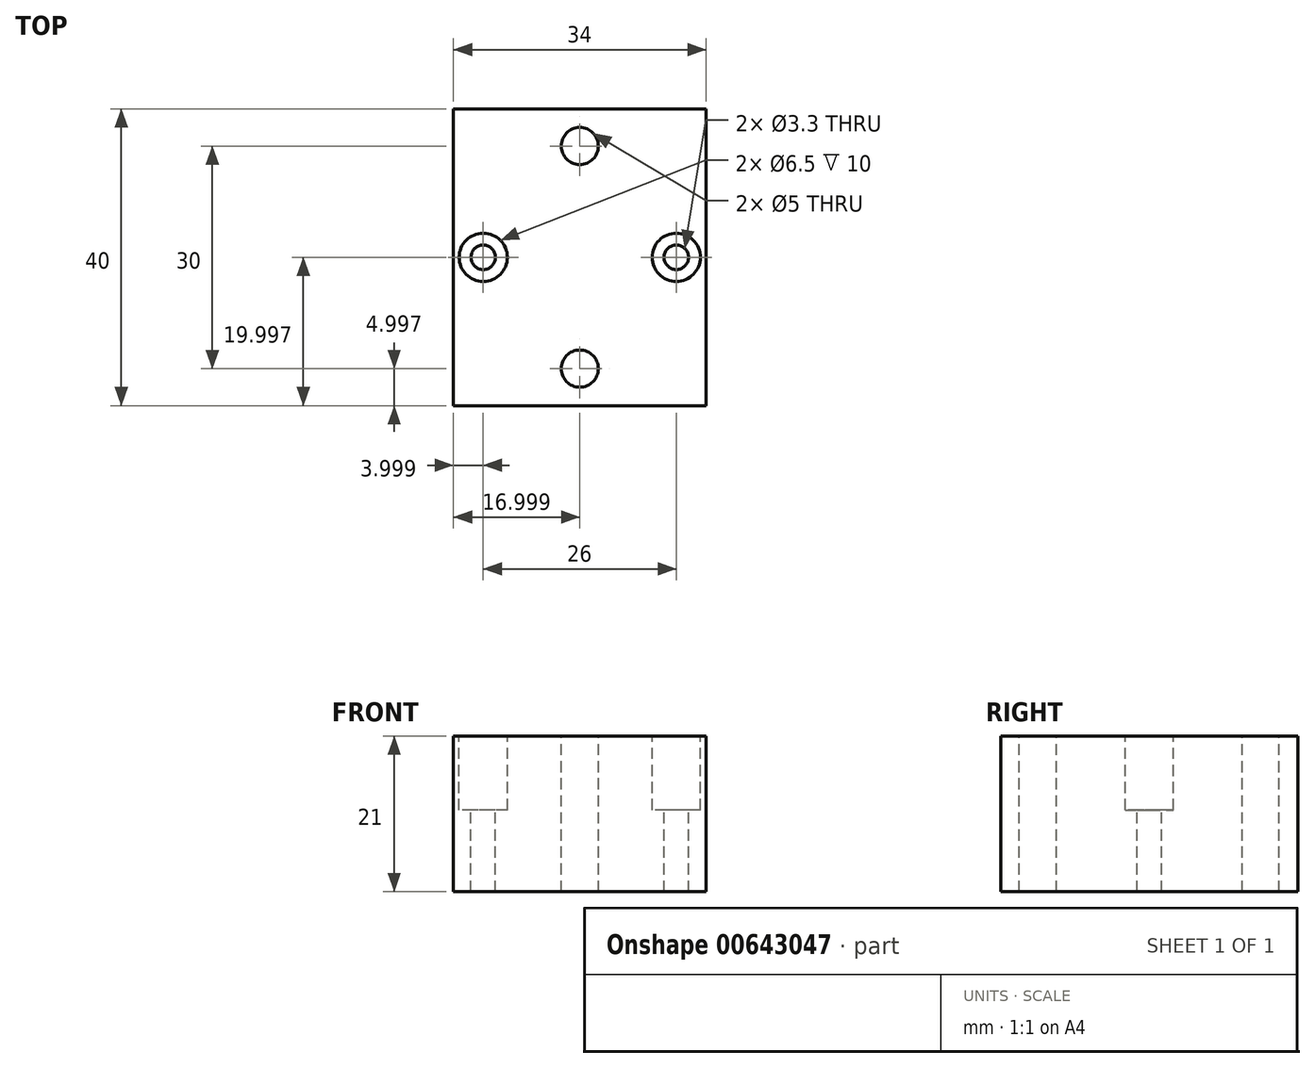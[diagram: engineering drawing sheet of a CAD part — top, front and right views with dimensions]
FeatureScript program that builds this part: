
annotation { "Feature Type Name" : "Feature", "Feature Type Description" : "" }
export const myFeature = defineFeature(function(context is Context, id is Id, definition is map)
    precondition{}
    {
        {
            var Q0;
            Q0=qCreatedBy(makeId("Top.planeOp"),FACE);
            var sketch = newSketch(context, id + "F0", { "sketchPlane" : qUnion([Q0])});
            skLineSegment(sketch, "E0.bottom", {"start": v(-36.8, -23.83) * mm, "end": v(-2.8, -23.83) * mm});
            skLineSegment(sketch, "E0.top", {"start": v(-36.8, -63.83) * mm, "end": v(-2.8, -63.83) * mm});
            skLineSegment(sketch, "E0.left", {"start": v(-36.8, -23.83) * mm, "end": v(-36.8, -63.83) * mm});
            skLineSegment(sketch, "E0.right", {"start": v(-2.8, -23.83) * mm, "end": v(-2.8, -63.83) * mm});
            skSolve(sketch);
        }
        {
            var Q0;
            Q0=makeQuery(id+"F0.imprint","IMPRINT",FACE,{"disambiguationData":[TD([[makeQuery(id+"F0.imprint","IMPRINT",EDGE,{"derivedFrom":sQuery(id+"F0.wireOp",EDGE,"E0.bottom")}),-1.0]])]});
            extrude(context, id + "F1", {"entities" : qUnion([Q0]), "depth" : 21 * mm});
        }
        {
            var Q0;
            Q0=makeQuery(id+"F1.opExtrude","CAP_FACE",FACE,{"disambiguationData":[OSD([sQuery(id+"F0.wireOp",EDGE,"E0.bottom"),sQuery(id+"F0.wireOp",EDGE,"E0.top"),sQuery(id+"F0.wireOp",EDGE,"E0.left"),sQuery(id+"F0.wireOp",EDGE,"E0.right")])],"isStart":false});
            var sketch = newSketch(context, id + "F2", { "sketchPlane" : qUnion([Q0])});
            skLineSegment(sketch, "E1", {"start": v(-19.8, -23.83) * mm, "end": v(-19.8, -63.83) * mm, "construction": true});
            skLineSegment(sketch, "E2", {"start": v(-36.8, -43.83) * mm, "end": v(-2.8, -43.83) * mm, "construction": true});
            skPoint(sketch, "E3", {"position": v(-19.8, -28.83) * mm});
            skPoint(sketch, "E4.MirrorP", {"position": v(-19.8, -58.83) * mm});
            skPoint(sketch, "E5", {"position": v(-32.8, -43.83) * mm});
            skPoint(sketch, "E6.MirrorP", {"position": v(-6.8, -43.83) * mm});
            skSolve(sketch);
        }
        {
            var Q0;
            Q0=sQuery(id+"F2.wireOp",VERTEX,"E5");
            var Q1;
            Q1=sQuery(id+"F2.wireOp",VERTEX,"E6.MirrorP");
            var Q2;
            Q2=makeQuery(id+"F1.opExtrude","SWEPT_BODY",BODY,{"disambiguationData":[OSD([sQuery(id+"F0.wireOp",EDGE,"E0.bottom"),sQuery(id+"F0.wireOp",EDGE,"E0.top"),sQuery(id+"F0.wireOp",EDGE,"E0.left"),sQuery(id+"F0.wireOp",EDGE,"E0.right")])]});
            hole(context, id + "F3", {"style" : HoleStyle.C_BORE, "endStyle" : HoleEndStyle.THROUGH, "holeDiameter" : 3.3 * mm, "cBoreDiameter" : 6.5 * mm, "cBoreDepth" : 10 * mm, "locations" : qUnion([Q0, Q1]), "scope" : qUnion([Q2]), "tappedDepth" : 12 * mm, "tapClearance" : 3});
        }
        {
            var Q0;
            Q0=sQuery(id+"F2.wireOp",VERTEX,"E3");
            var Q1;
            Q1=sQuery(id+"F2.wireOp",VERTEX,"E4.MirrorP");
            var Q2;
            Q2=makeQuery(id+"F1.opExtrude","SWEPT_BODY",BODY,{"disambiguationData":[OSD([sQuery(id+"F0.wireOp",EDGE,"E0.bottom"),sQuery(id+"F0.wireOp",EDGE,"E0.top"),sQuery(id+"F0.wireOp",EDGE,"E0.left"),sQuery(id+"F0.wireOp",EDGE,"E0.right")])]});
            hole(context, id + "F4", {"style" : HoleStyle.SIMPLE, "endStyle" : HoleEndStyle.THROUGH, "standardTappedOrClearance" : lookupTablePath({ "standard" : "ISO", "engagement" : "75%", "pitch" : "1 mm", "size" : "M6", "type" : "Tapped" }), "standardBlindInLast" : lookupTablePath({ "standard" : "ISO", "engagement" : "75%", "pitch" : "1 mm", "size" : "M6", "type" : "Tapped" }), "holeDiameter" : 5 * mm, "locations" : qUnion([Q0, Q1]), "scope" : qUnion([Q2]), "tappedDepth" : 12 * mm, "tapClearance" : 3, "majorDiameter" : 6 * mm});
        }
    });
